# Revit family: Mop_Sink-Willoughby-WMS-242412
name_source: partatom
category: Plumbing Fixtures
revit_build: Autodesk Revit 2015 (Build: 20140606_1530(x64)
units: mm (PartAtom-declared; Revit-internal decimal feet)

## types (6) — shared parameters
CW Connection = No
Default Elevation = 0' - 0"
Fixture Body = Stainless Steel AISI 304-Willoughby
HW Connection = No
Manufacturer = Willoughby Industries
Revision = A
Vent Connection = No
Waste Connection = Yes
Waste DIA = 2"

## per-type parameters (varying)
| type | Depth | Description | Drain Depth | Height | Model | URL | Void Height | Width |
| 24246 | 2' - 0" | Mop Sink | 1' - 0" | 0' - 6" | CWMS-24246 | www.willoughby-ind.com | 0' - 5 13/16" | 2' - 0" |
| 242412 | 2' - 0" | Mop Sink, 24" X 24" X 12" | 1' - 0" | 1' - 0" | WMS-242412 | https://www.willoughby-ind.com | 0' - 11 13/16" | 2' - 0" |
| 32326 | 2' - 8" | Mop Sink | 1' - 4" | 0' - 6" | CWMS-32326 | www.willoughby-ind.com | 0' - 5 13/16" | 2' - 8" |
| 323212 | 2' - 8" | Mop Sink | 1' - 4" | 1' - 0" | CWMS-323212 | www.willoughby-ind.com | 0' - 11 13/16" | 2' - 8" |
| 36366 | 3' - 0" | Mop Sink | 1' - 6" | 0' - 6" | CWMS-36366 | www.willoughby-ind.com | 0' - 5 13/16" | 3' - 0" |
| 363612 | 3' - 0" | Mop Sink | 1' - 6" | 1' - 0" | CWMS-363612 | www.willoughby-ind.com | 0' - 11 13/16" | 3' - 0" |

## geometry (parser evidence)
native form markers: Sweep x2
no freeform markers — native parametric forms only
